# Revit family: FU_Inspec_Grade_1-12
name_source: partatom
category: Furniture
units: mm (PartAtom-declared; Revit-internal decimal feet)

## family parameters
Always vertical = Yes
Cut with Voids When Loaded = No
OmniClass Number = 23.40.20.00
OmniClass Title = General Furniture and Specialties
Room Calculation Point = No
Shared = No
Work Plane-Based = No

## types (3) — shared parameters
Assembly Code = E2020
Depth = 540 mm  [stored 1.77165 ft]
Description = Chair with recycled polypropylene seat on a powder coated or chromium plated tubular steel frame. Stackable and linkable
Height = 780 mm  [stored 2.55906 ft]
Keynote = 46.B
Manufacturer = Inspec
Model = Grade 1.1
Seat Pad Material = Fabric - Divina Red
URL = https://inspecfurniture.com
Weight = 4.5
Width = 510 mm  [stored 1.67323 ft]
zero-valued in all types: Default Elevation

## per-type parameters (varying)
| type | Frame Material | Seat Material |
| Grade 1.10 - White - White | Metal - White - Matte | Plastic - White |
| Grade 1.11 - Graphite - Black | Metal - Graphite - Matte | Plastic - Black |
| Grade 1.12 - Chrome - Beige | Metal - Chrome - Polished | Fabric - Divina Beige |

note: [stored X ft] marks values corroborated as IEEE doubles in the binary element streams (Revit-internal decimal feet)

## geometry (parser evidence)
native form markers: Blend x417, Sweep x2
no freeform markers — native parametric forms only
